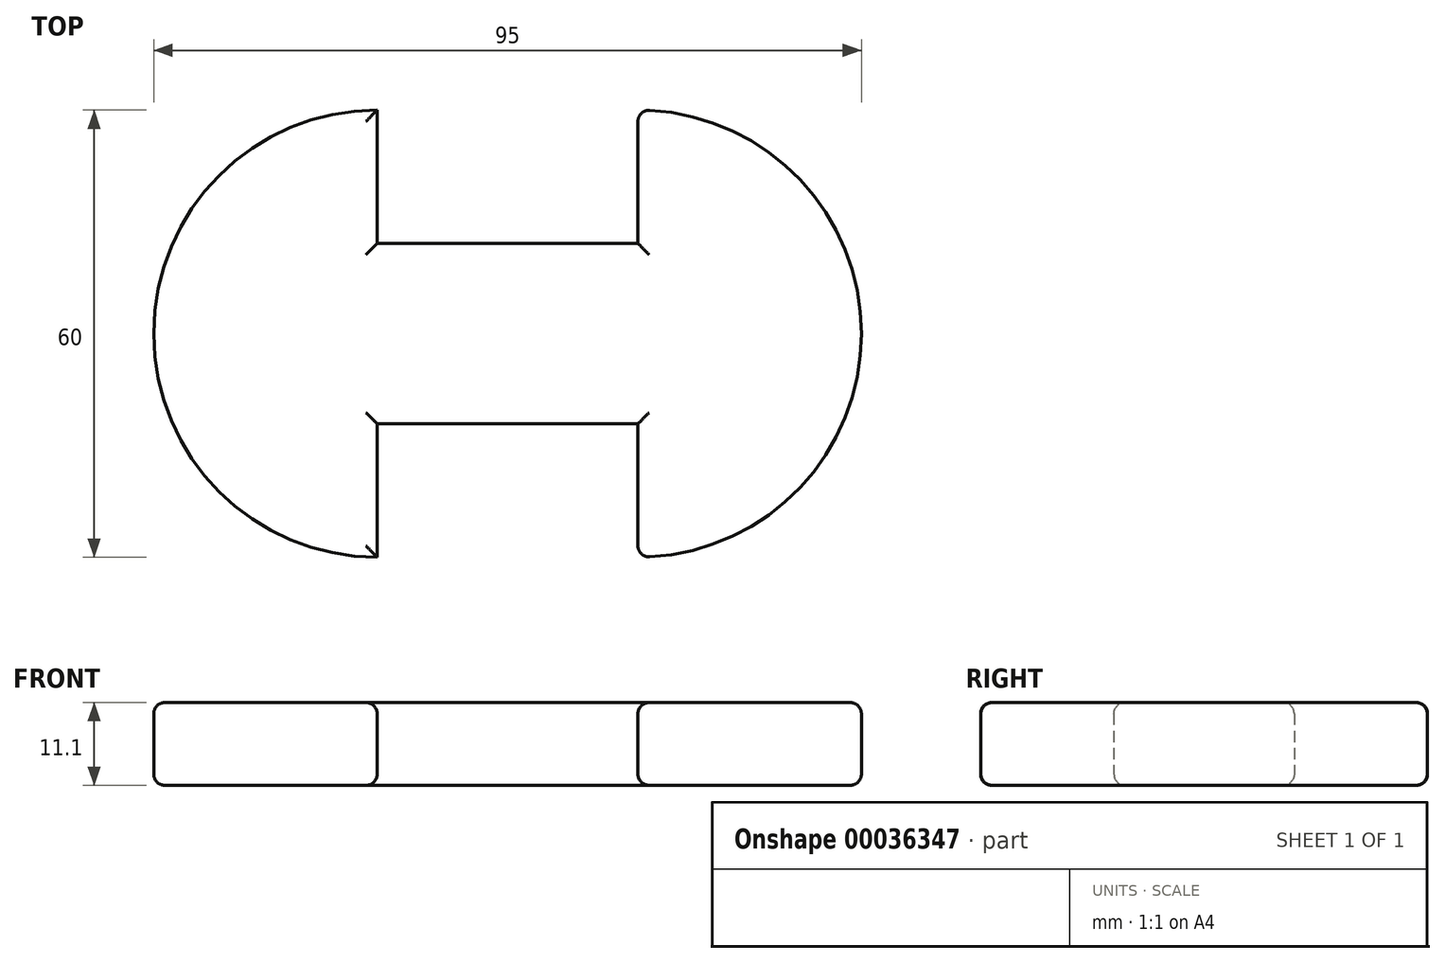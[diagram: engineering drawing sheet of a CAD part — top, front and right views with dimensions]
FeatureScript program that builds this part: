
annotation { "Feature Type Name" : "Feature", "Feature Type Description" : "" }
export const myFeature = defineFeature(function(context is Context, id is Id, definition is map)
    precondition{}
    {
        {
            var Q0;
            Q0=qCreatedBy(makeId("Top.planeOp"),FACE);
            var sketch = newSketch(context, id + "F0", { "sketchPlane" : qUnion([Q0])});
            skLineSegment(sketch, "E0.rect.bottom", {"start": v(17.5, 12.1) * mm, "end": v(-17.5, 12.1) * mm});
            skLineSegment(sketch, "E0.rect.top", {"start": v(17.5, -12.1) * mm, "end": v(-17.5, -12.1) * mm});
            skLineSegment(sketch, "E0.rect.left", {"start": v(17.5, 12.1) * mm, "end": v(17.5, -12.1) * mm});
            skLineSegment(sketch, "E0.rect.right", {"start": v(-17.5, 12.1) * mm, "end": v(-17.5, -12.1) * mm});
            skPoint(sketch, "E0.rect.middle", {"position": v(0, 0) * mm});
            skArc(sketch, "E1", {"start": v(-17.5, 30) * mm, "mid": v(-47.5, 0) * mm, "end": v(-17.5, -30) * mm});
            skLineSegment(sketch, "E2", {"start": v(-17.5, 30) * mm, "end": v(-17.5, -30) * mm});
            skArc(sketch, "E3", {"start": v(17.5, -30) * mm, "mid": v(47.5, 0) * mm, "end": v(17.5, 30) * mm});
            skLineSegment(sketch, "E4", {"start": v(17.5, 30) * mm, "end": v(17.5, -30) * mm});
            skSolve(sketch);
        }
        {
            var Q0;
            {var subQ1=sQuery(id+"F0.wireOp",EDGE,"E1");Q0=makeQuery(id+"F0.imprint","IMPRINT",FACE,{"disambiguationData":[TD([[makeQuery(id+"F0.imprint","IMPRINT",EDGE,{"derivedFrom":subQ1}),1.0]])]});}
            var Q1;
            {var subQ1=sQuery(id+"F0.wireOp",EDGE,"E3");Q1=makeQuery(id+"F0.imprint","IMPRINT",FACE,{"disambiguationData":[TD([[makeQuery(id+"F0.imprint","IMPRINT",EDGE,{"derivedFrom":subQ1}),1.0]])]});}
            var Q2;
            {var subQ2=sQuery(id+"F0.wireOp",EDGE,"E0.rect.bottom");Q2=makeQuery(id+"F0.imprint","IMPRINT",FACE,{"disambiguationData":[TD([[makeQuery(id+"F0.imprint","IMPRINT",EDGE,{"derivedFrom":subQ2}),1.0]])]});}
            extrude(context, id + "F1", {"entities" : qUnion([Q0, Q1, Q2]), "depth" : 11.1 * mm});
        }
        {
            var Q0;
            Q0=makeQuery(id+"F1.opExtrude","CAP_EDGE",EDGE,{"disambiguationData":[OSD([sQuery(id+"F0.wireOp",EDGE,"E1")])],"isStart":false});
            var Q1;
            Q1=makeQuery(id+"F1.opExtrude","CAP_FACE",FACE,{"disambiguationData":[OSD([sQuery(id+"F0.wireOp",EDGE,"E0.rect.bottom"),sQuery(id+"F0.wireOp",EDGE,"E0.rect.top"),sQuery(id+"F0.wireOp",EDGE,"E1"),sQuery(id+"F0.wireOp",EDGE,"E2"),sQuery(id+"F0.wireOp",EDGE,"E3"),sQuery(id+"F0.wireOp",EDGE,"E4")])],"isStart":false});
            var Q2;
            Q2=makeQuery(id+"F1.opExtrude","CAP_FACE",FACE,{"disambiguationData":[OSD([sQuery(id+"F0.wireOp",EDGE,"E0.rect.bottom"),sQuery(id+"F0.wireOp",EDGE,"E0.rect.top"),sQuery(id+"F0.wireOp",EDGE,"E1"),sQuery(id+"F0.wireOp",EDGE,"E2"),sQuery(id+"F0.wireOp",EDGE,"E3"),sQuery(id+"F0.wireOp",EDGE,"E4")])],"isStart":true});
            var Q3;
            Q3=makeQuery(id+"F1.opExtrude","SWEPT_FACE",FACE,{"disambiguationData":[OSD([sQuery(id+"F0.wireOp",EDGE,"E3")])]});
            fillet(context, id + "F2", {"entities" : qUnion([Q0, Q1, Q2, Q3]), "radius" : 1.5 * mm, "tangentPropagation" : true, "allowEdgeOverflow" : false});
        }
    });
